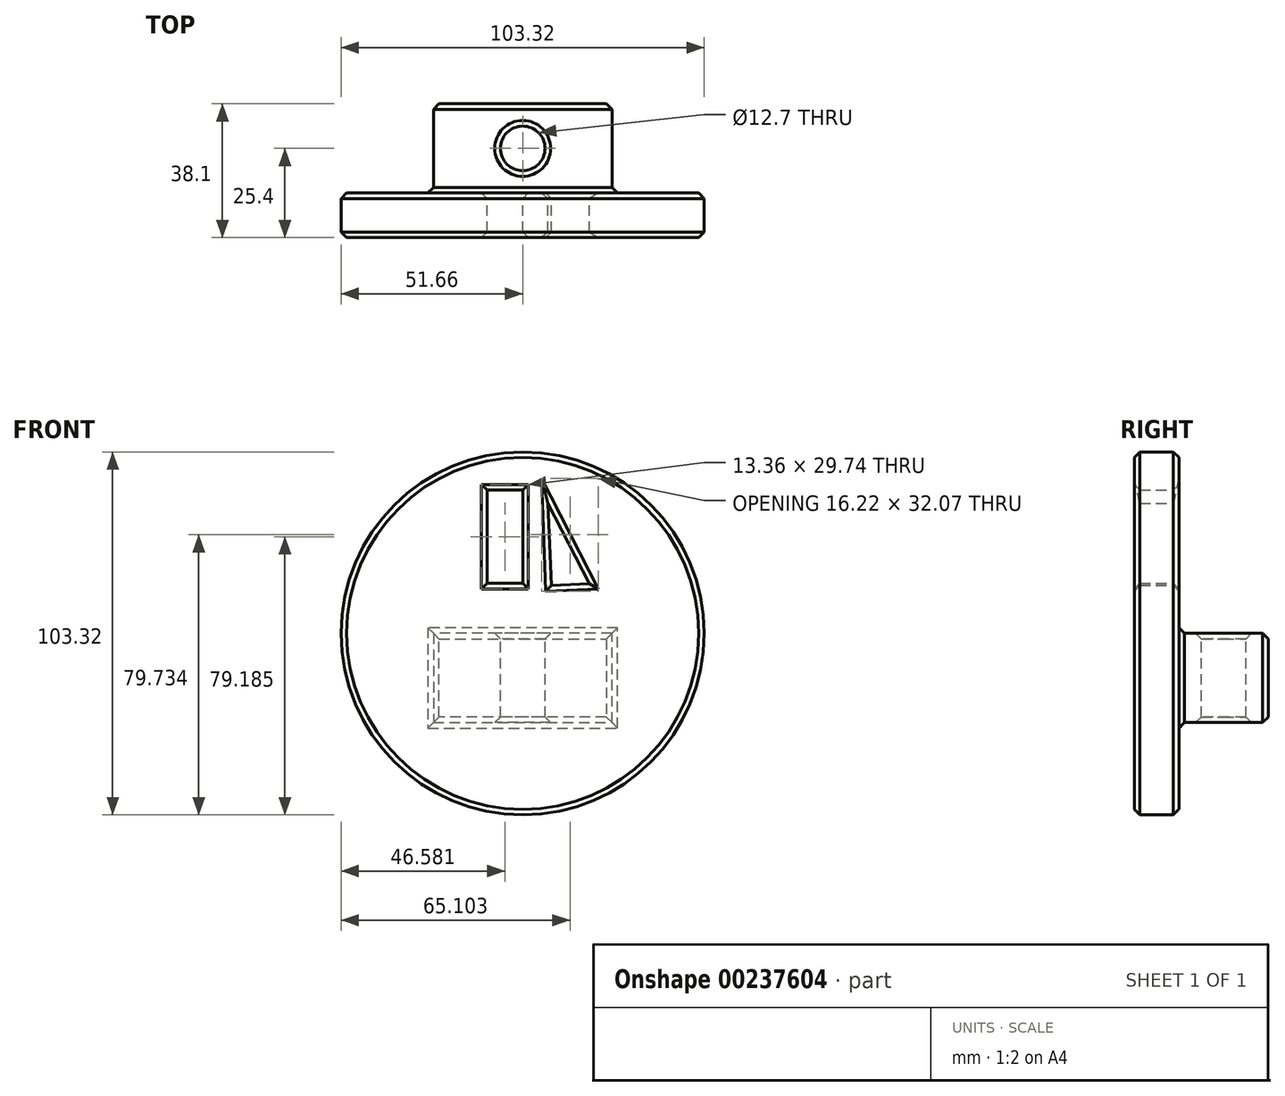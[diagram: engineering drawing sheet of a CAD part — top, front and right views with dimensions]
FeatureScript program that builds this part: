
annotation { "Feature Type Name" : "Feature", "Feature Type Description" : "" }
export const myFeature = defineFeature(function(context is Context, id is Id, definition is map)
    precondition{}
    {
        {
            var Q0;
            Q0=qCreatedBy(makeId("Front.planeOp"),FACE);
            var sketch = newSketch(context, id + "F0", { "sketchPlane" : qUnion([Q0])});
            skCircle(sketch, "E0", {"center": v(0, 0) * mm, "radius": 51.66 * mm});
            skLineSegment(sketch, "E1.bottom", {"start": v(0, 14.25) * mm, "end": v(-10.16, 14.25) * mm});
            skLineSegment(sketch, "E1.top", {"start": v(0, 40.8) * mm, "end": v(-10.16, 40.8) * mm});
            skLineSegment(sketch, "E1.left", {"start": v(0, 14.25) * mm, "end": v(0, 40.8) * mm});
            skLineSegment(sketch, "E1.right", {"start": v(-10.16, 14.25) * mm, "end": v(-10.16, 40.8) * mm});
            skLineSegment(sketch, "E2", {"start": v(8.12, 13.7) * mm, "end": v(7.1, 39.75) * mm});
            skLineSegment(sketch, "E3", {"start": v(8.12, 13.7) * mm, "end": v(18.98, 14.12) * mm});
            skLineSegment(sketch, "E4", {"start": v(18.98, 14.12) * mm, "end": v(7.21, 36.97) * mm});
            skSolve(sketch);
        }
        {
            var Q0;
            Q0 = qSketchRegion(id + "F0", true);
            extrude(context, id + "F1", {"entities" : qUnion([Q0]), "depth" : 12.7 * mm});
        }
        {
            var Q0;
            Q0=qCreatedBy(makeId("Top.planeOp"),FACE);
            var sketch = newSketch(context, id + "F2", { "sketchPlane" : qUnion([Q0])});
            skLineSegment(sketch, "E5.bottom", {"start": v(-23.81, 0) * mm, "end": v(25.4, 0) * mm});
            skLineSegment(sketch, "E5.top", {"start": v(-25.4, 25.4) * mm, "end": v(25.4, 25.4) * mm});
            skLineSegment(sketch, "E5.left", {"start": v(-25.4, 1.59) * mm, "end": v(-25.4, 25.4) * mm});
            skLineSegment(sketch, "E5.right", {"start": v(25.4, 0) * mm, "end": v(25.4, 25.4) * mm});
            skPoint(sketch, "E6.visualSharp", {"position": v(-25.4, 0) * mm});
            skArc(sketch, "E6.filletArc", {"start": v(-25.4, 1.59) * mm, "mid": v(-24.94, 0.46) * mm, "end": v(-23.81, 0) * mm});
            skCircle(sketch, "E7", {"center": v(0, 12.7) * mm, "radius": 6.35 * mm});
            skSolve(sketch);
        }
        {
            var Q0;
            Q0 = qSketchRegion(id + "F2", true);
            extrude(context, id + "F3", {"entities" : qUnion([Q0]), "operationType" : NewBodyOperationType.ADD, "oppositeDirection" : true, "depth" : 25.4 * mm});
        }
        {
            var Q0;
            Q0=makeQuery(id+"F1.opExtrude","CAP_EDGE",EDGE,{"disambiguationData":[OSD([sQuery(id+"F0.wireOp",EDGE,"E0")])],"isStart":true});
            var Q1;
            Q1=makeQuery(id+"F1.opExtrude","CAP_FACE",FACE,{"disambiguationData":[OSD([sQuery(id+"F0.wireOp",EDGE,"E0"),sQuery(id+"F0.wireOp",EDGE,"E1.bottom"),sQuery(id+"F0.wireOp",EDGE,"E1.top"),sQuery(id+"F0.wireOp",EDGE,"E1.left"),sQuery(id+"F0.wireOp",EDGE,"E1.right"),sQuery(id+"F0.wireOp",EDGE,"E2"),sQuery(id+"F0.wireOp",EDGE,"E3"),sQuery(id+"F0.wireOp",EDGE,"E4")])],"isStart":true});
            chamfer(context, id + "F4", {"entities" : qUnion([Q0, Q1]), "width" : 1.6 * mm, "tangentPropagation" : true});
        }
        {
            var Q0;
            Q0=makeQuery(id+"F3.opExtrude","CAP_EDGE",EDGE,{"disambiguationData":[OSD([sQuery(id+"F2.wireOp",EDGE,"E7")])],"isStart":false});
            chamfer(context, id + "F5", {"entities" : qUnion([Q0]), "width" : 1.6 * mm, "tangentPropagation" : true});
        }
        {
            var Q0;
            Q0=makeQuery(id+"F1.opExtrude","CAP_EDGE",EDGE,{"disambiguationData":[OSD([sQuery(id+"F0.wireOp",EDGE,"E0")])],"isStart":false});
            var Q1;
            Q1=makeQuery(id+"F1.opExtrude","CAP_FACE",FACE,{"disambiguationData":[OSD([sQuery(id+"F0.wireOp",EDGE,"E0"),sQuery(id+"F0.wireOp",EDGE,"E1.bottom"),sQuery(id+"F0.wireOp",EDGE,"E1.top"),sQuery(id+"F0.wireOp",EDGE,"E1.left"),sQuery(id+"F0.wireOp",EDGE,"E1.right"),sQuery(id+"F0.wireOp",EDGE,"E2"),sQuery(id+"F0.wireOp",EDGE,"E3"),sQuery(id+"F0.wireOp",EDGE,"E4")])],"isStart":false});
            chamfer(context, id + "F6", {"entities" : qUnion([Q0, Q1]), "width" : 1.6 * mm, "tangentPropagation" : true});
        }
        {
            var Q0;
            Q0=makeQuery(id+"F3.opExtrude","CAP_EDGE",EDGE,{"disambiguationData":[OSD([sQuery(id+"F2.wireOp",EDGE,"E7")])],"isStart":true});
            chamfer(context, id + "F7", {"entities" : qUnion([Q0]), "width" : 1.6 * mm, "tangentPropagation" : true});
        }
        {
            var Q0;
            Q0=makeQuery(id+"F3.opExtrude","SWEPT_FACE",FACE,{"disambiguationData":[OSD([sQuery(id+"F2.wireOp",EDGE,"E5.top")])]});
            chamfer(context, id + "F8", {"entities" : qUnion([Q0]), "width" : 1.6 * mm, "tangentPropagation" : true});
        }
    });
